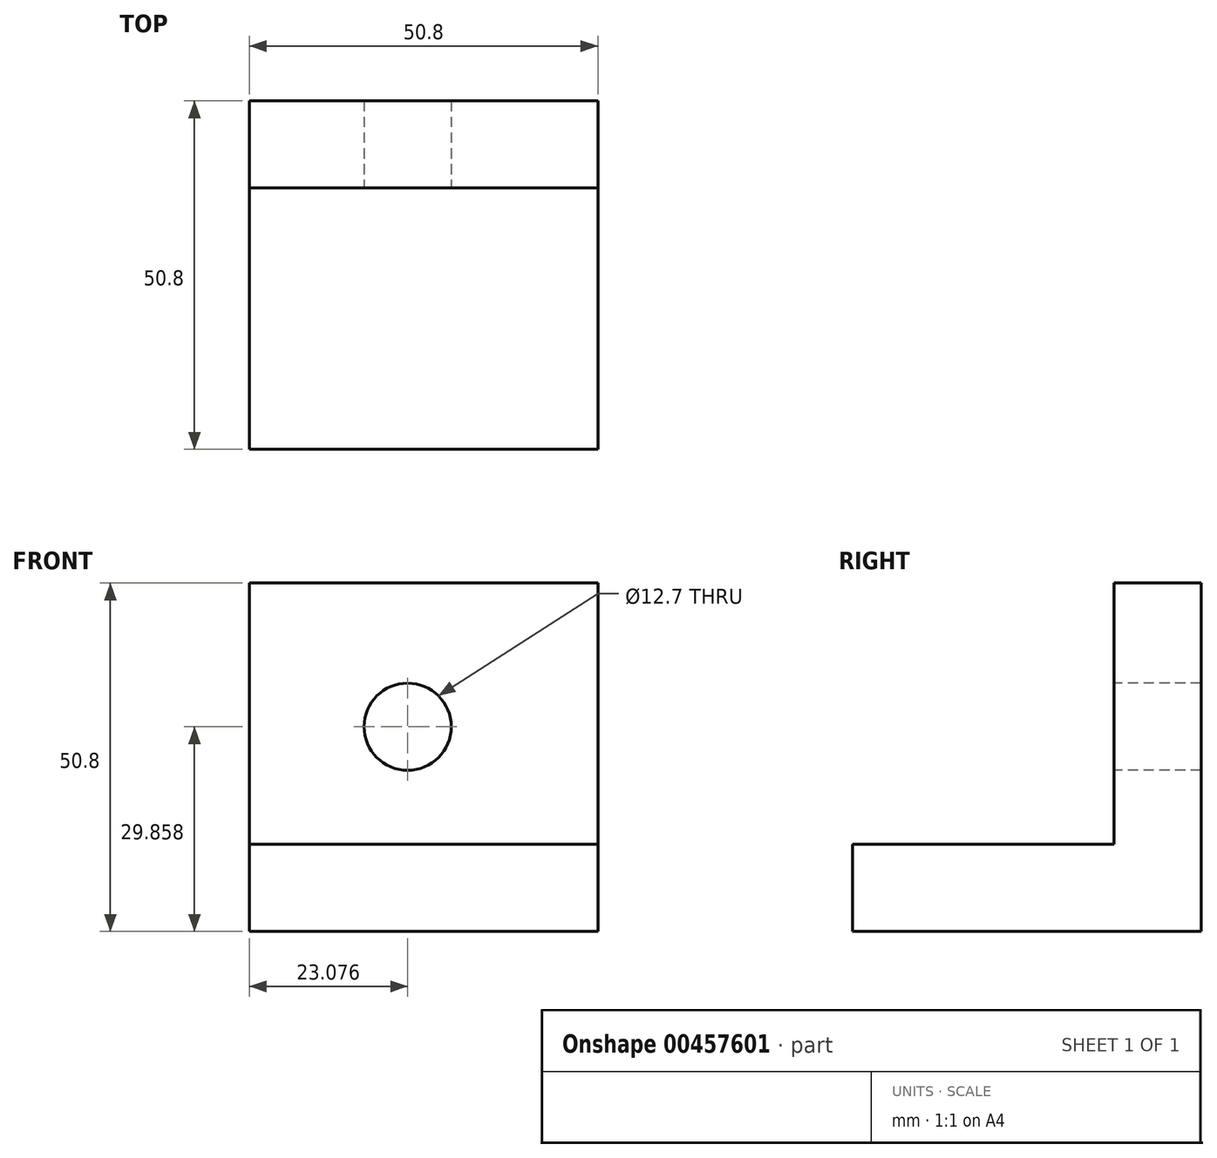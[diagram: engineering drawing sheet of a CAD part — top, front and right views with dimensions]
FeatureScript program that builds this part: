
annotation { "Feature Type Name" : "Feature", "Feature Type Description" : "" }
export const myFeature = defineFeature(function(context is Context, id is Id, definition is map)
    precondition{}
    {
        {
            var Q0;
            Q0=qCreatedBy(makeId("Top.planeOp"),FACE);
            var sketch = newSketch(context, id + "F0", { "sketchPlane" : qUnion([Q0])});
            skLineSegment(sketch, "E0.bottom", {"start": v(-15.45, 11.05) * mm, "end": v(35.35, 11.05) * mm});
            skLineSegment(sketch, "E0.top", {"start": v(-15.45, -39.75) * mm, "end": v(35.35, -39.75) * mm});
            skLineSegment(sketch, "E0.left", {"start": v(-15.45, 11.05) * mm, "end": v(-15.45, -39.75) * mm});
            skLineSegment(sketch, "E0.right", {"start": v(35.35, 11.05) * mm, "end": v(35.35, -39.75) * mm});
            skLineSegment(sketch, "E1", {"start": v(-15.45, -1.65) * mm, "end": v(35.35, -1.65) * mm});
            skSolve(sketch);
        }
        {
            var Q0;
            {var subQ0=sQuery(id+"F0.wireOp",EDGE,"E0.top");Q0=makeQuery(id+"F0.imprint","IMPRINT",FACE,{"disambiguationData":[TD([[makeQuery(id+"F0.imprint","IMPRINT",EDGE,{"derivedFrom":subQ0}),1.0]])]});}
            extrude(context, id + "F1", {"entities" : qUnion([Q0]), "depth" : 12.7 * mm});
        }
        {
            var Q0;
            {var subQ0=sQuery(id+"F0.wireOp",EDGE,"E0.bottom");Q0=makeQuery(id+"F0.imprint","IMPRINT",FACE,{"disambiguationData":[TD([[makeQuery(id+"F0.imprint","IMPRINT",EDGE,{"derivedFrom":subQ0}),-1.0]])]});}
            extrude(context, id + "F2", {"entities" : qUnion([Q0]), "operationType" : NewBodyOperationType.ADD, "depth" : 50.8 * mm});
        }
        {
            var Q0;
            Q0=makeQuery(id+"F2.opExtrude","SWEPT_FACE",FACE,{"disambiguationData":[OSD([sQuery(id+"F0.wireOp",EDGE,"E1")])]});
            var sketch = newSketch(context, id + "F3", { "sketchPlane" : qUnion([Q0])});
            skCircle(sketch, "E2", {"center": v(7.63, 29.86) * mm, "radius": 6.35 * mm});
            skSolve(sketch);
        }
        {
            var Q0;
            Q0 = qSketchRegion(id + "F3", true);
            extrude(context, id + "F4", {"entities" : qUnion([Q0]), "operationType" : NewBodyOperationType.REMOVE, "oppositeDirection" : true, "depth" : 25.4 * mm});
        }
    });
